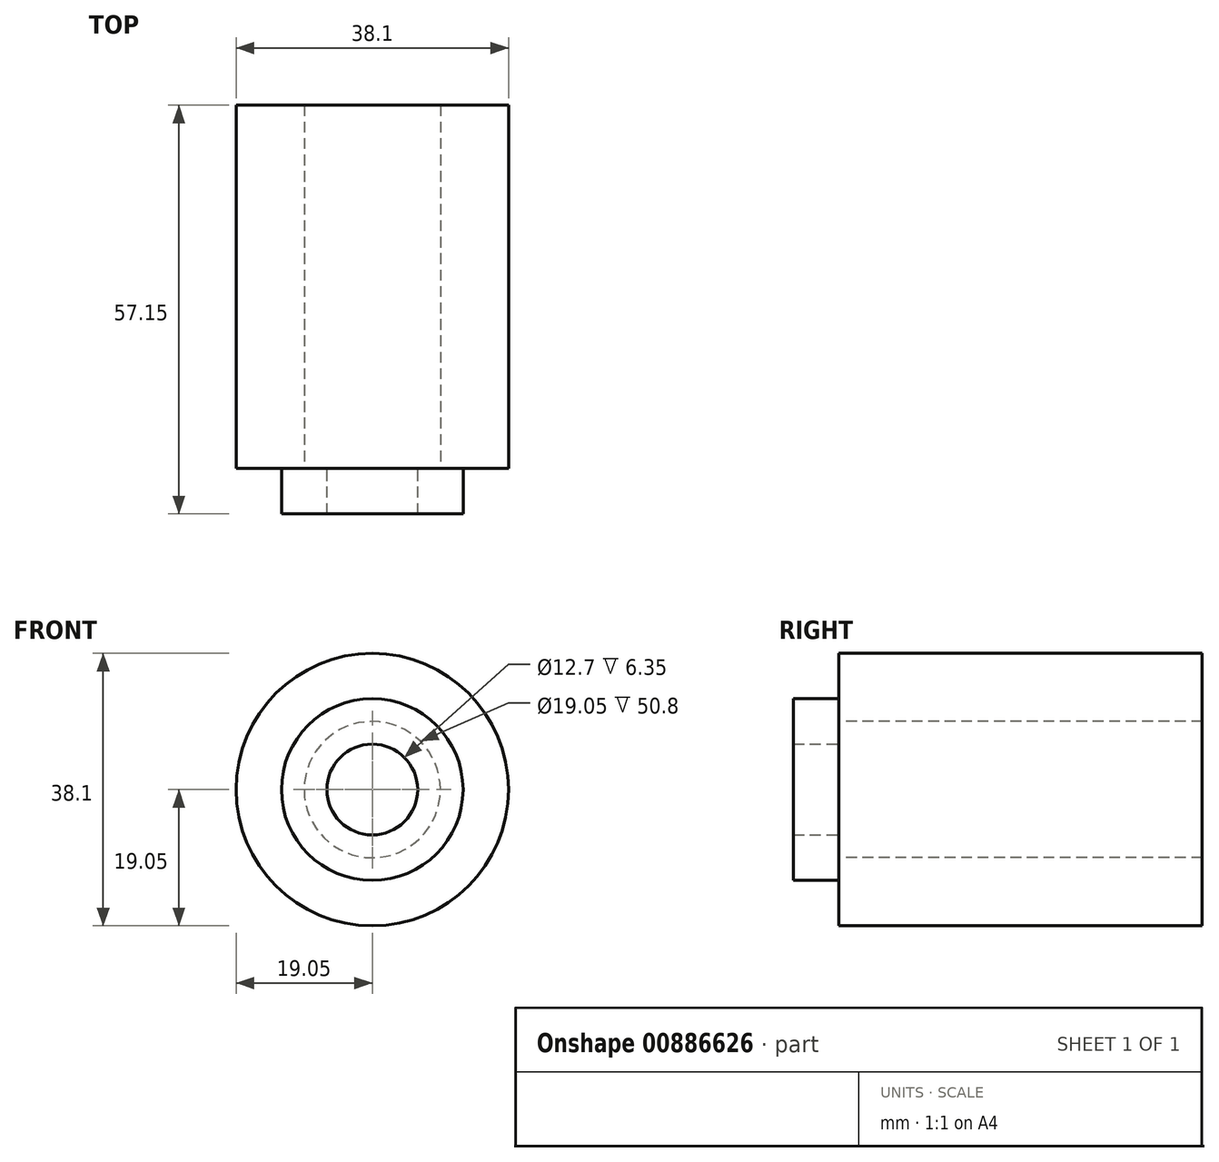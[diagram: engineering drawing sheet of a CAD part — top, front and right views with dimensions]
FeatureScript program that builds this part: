
annotation { "Feature Type Name" : "Feature", "Feature Type Description" : "" }
export const myFeature = defineFeature(function(context is Context, id is Id, definition is map)
    precondition{}
    {
        {
            assignVariable(context, id + "F0", {"name" : "height1", "anyValue" : 6.35 * mm});
        }
        {
            assignVariable(context, id + "F1", {"name" : "height2", "anyValue" : 50.8 * mm});
        }
        {
            var Q0;
            Q0=qCreatedBy(makeId("Front.planeOp"),FACE);
            var sketch = newSketch(context, id + "F2", { "sketchPlane" : qUnion([Q0])});
            skCircle(sketch, "E0", {"center": v(0, 0) * mm, "radius": 12.7 * mm});
            skCircle(sketch, "E1", {"center": v(0, 0) * mm, "radius": 6.35 * mm});
            skSolve(sketch);
        }
        {
            var Q0;
            Q0=makeQuery(id+"F2.imprint","IMPRINT",FACE,{"disambiguationData":[TD([[makeQuery(id+"F2.imprint","IMPRINT",EDGE,{"derivedFrom":sQuery(id+"F2.wireOp",EDGE,"E0")}),1.0]])]});
            extrude(context, id + "F3", {"entities" : qUnion([Q0]), "depth" : getVariable(context, 'height1'), "offsetDistance" : 25.4 * mm});
        }
        {
            var Q0;
            Q0=qCreatedBy(makeId("Front.planeOp"),FACE);
            var sketch = newSketch(context, id + "F4", { "sketchPlane" : qUnion([Q0])});
            skCircle(sketch, "E2", {"center": v(0, 0) * mm, "radius": 19.05 * mm});
            skCircle(sketch, "E3", {"center": v(0, 0) * mm, "radius": 9.53 * mm});
            skSolve(sketch);
        }
        {
            var Q0;
            Q0=makeQuery(id+"F4.imprint","IMPRINT",FACE,{"disambiguationData":[TD([[makeQuery(id+"F4.imprint","IMPRINT",EDGE,{"derivedFrom":sQuery(id+"F4.wireOp",EDGE,"E2")}),1.0]])]});
            extrude(context, id + "F5", {"entities" : qUnion([Q0]), "operationType" : NewBodyOperationType.ADD, "oppositeDirection" : true, "depth" : getVariable(context, 'height2'), "offsetDistance" : 25.4 * mm});
        }
    });
